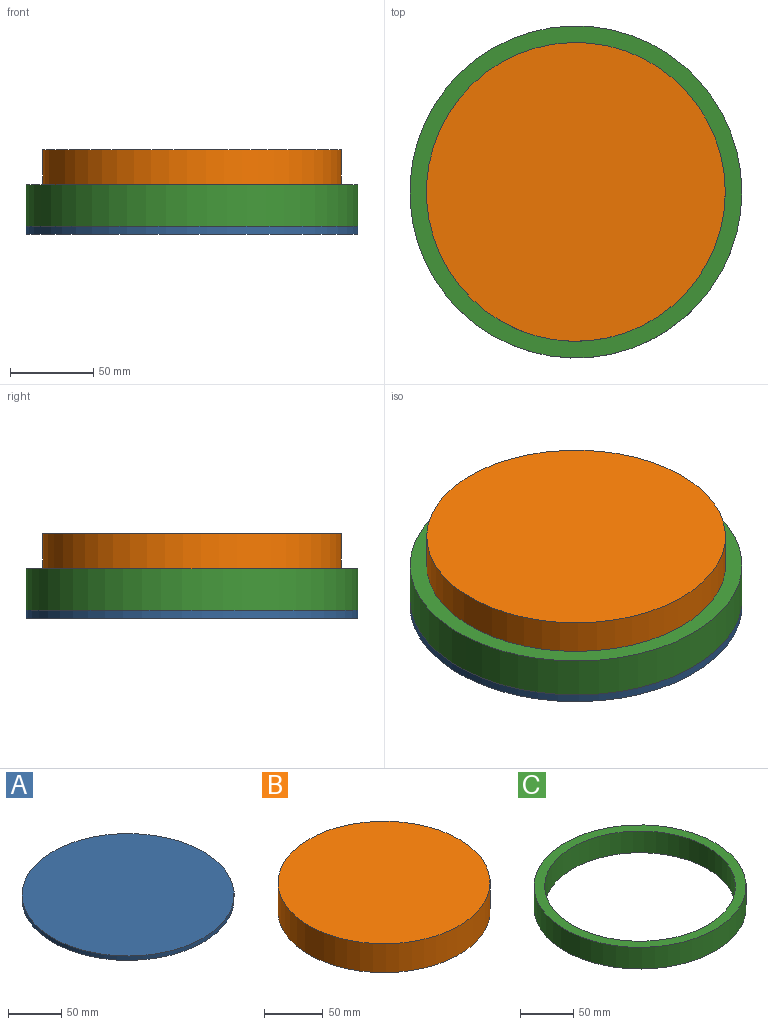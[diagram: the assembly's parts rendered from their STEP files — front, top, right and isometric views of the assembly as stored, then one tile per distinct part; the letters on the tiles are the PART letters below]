
ASSEMBLY  parts=3 mates=2
PART A: 3 faces, bbox 200x200x5 mm
  f0: cylinder r=100mm len=200mm, axis (0,0,-1), area 3141.6mm2, adj f1,f2
  f1: plane 200x200mm, normal (0,0,1), area 31415.9mm2, adj f0
  f2: plane 200x200mm, normal (0,0,-1), area 31415.9mm2, adj f0
PART B: 3 faces, bbox 180x180x30 mm
  f0: cylinder r=90mm len=180mm, axis (0,0,-1), area 16964.6mm2, adj f1,f2
  f1: plane 180x180mm, normal (0,0,1), area 25446.9mm2, adj f0
  f2: plane 180x180mm, normal (0,0,-1), area 25446.9mm2, adj f0
PART C: 4 faces, bbox 200x200x25 mm
  f0: cylinder r=90mm len=180mm, axis (0,0,-1), area 14137.2mm2, adj f2,f3
  f1: cylinder r=100mm len=200mm, axis (0,0,-1), area 15708mm2, adj f2,f3
  f2: plane 200x200mm, normal (0,0,1), area 5969mm2, adj f0,f1
  f3: plane 200x200mm, normal (0,0,-1), area 5969mm2, adj f0,f1
PLACE A rot(axis=(0.2,-0.96,0.18),0deg) t=(-27.73,-3.6,-11.76)mm
PLACE B rot(axis=(0.2,-0.96,0.18),0deg) t=(-27.73,-3.6,9.34)mm
PLACE C rot(axis=(0.2,-0.96,0.18),0deg) t=(-27.73,-3.6,-6.76)mm
MATE slider B.f0 <-> C.f0  axis (0,0,-1) through (-27.73,-3.6,9.34)mm
MATE fastened C.f1 <-> A.f0  axis (0,0,-1) through (-27.73,-3.6,-6.76)mm
